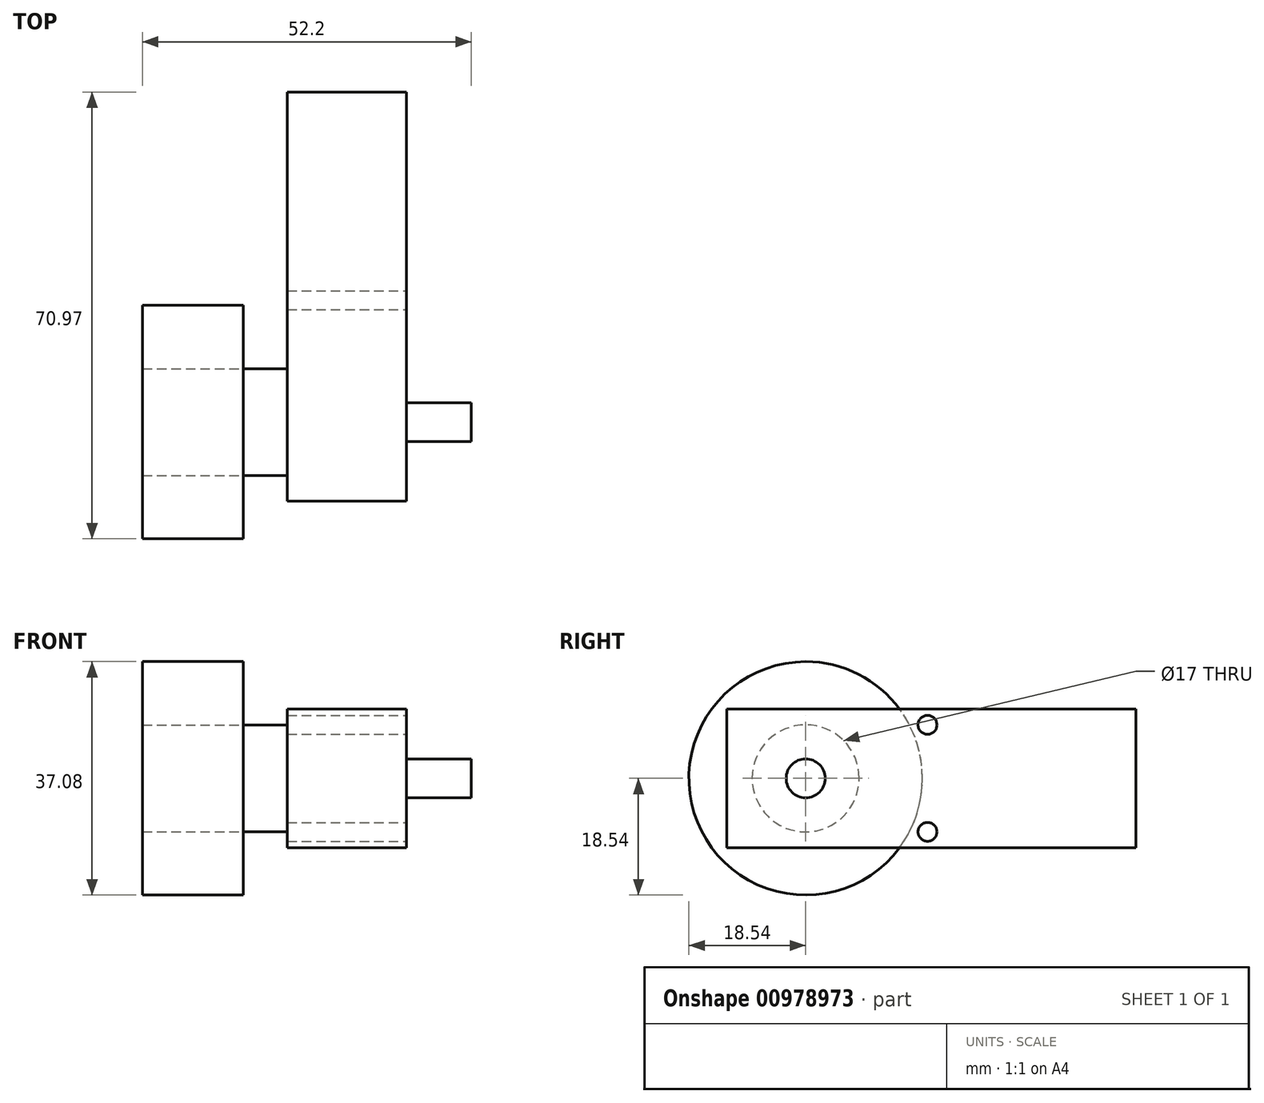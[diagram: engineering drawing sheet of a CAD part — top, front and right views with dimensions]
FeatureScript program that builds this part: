
annotation { "Feature Type Name" : "Feature", "Feature Type Description" : "" }
export const myFeature = defineFeature(function(context is Context, id is Id, definition is map)
    precondition{}
    {
        {
            var Q0;
            Q0=qCreatedBy(makeId("Top.planeOp"),FACE);
            var sketch = newSketch(context, id + "F0", { "sketchPlane" : qUnion([Q0])});
            skLineSegment(sketch, "E0.bottom", {"start": v(-11.97, 42.12) * mm, "end": v(6.93, 42.12) * mm});
            skLineSegment(sketch, "E0.top", {"start": v(-11.97, -22.86) * mm, "end": v(6.93, -22.86) * mm});
            skLineSegment(sketch, "E0.left", {"start": v(-11.97, 42.12) * mm, "end": v(-11.97, -22.86) * mm});
            skLineSegment(sketch, "E0.right", {"start": v(6.93, 42.12) * mm, "end": v(6.93, -22.86) * mm});
            skSolve(sketch);
        }
        {
            var Q0;
            Q0=makeQuery(id+"F0.imprint","IMPRINT",FACE,{"disambiguationData":[TD([[makeQuery(id+"F0.imprint","IMPRINT",EDGE,{"derivedFrom":sQuery(id+"F0.wireOp",EDGE,"E0.bottom")}),-1.0]])]});
            extrude(context, id + "F1", {"entities" : qUnion([Q0]), "depth" : 22 * mm, "offsetDistance" : 25 * mm});
        }
        {
            var Q0;
            Q0=makeQuery(id+"F1.opExtrude","SWEPT_FACE",FACE,{"disambiguationData":[OSD([sQuery(id+"F0.wireOp",EDGE,"E0.left")])]});
            var sketch = newSketch(context, id + "F2", { "sketchPlane" : qUnion([Q0])});
            skCircle(sketch, "E1", {"center": v(10.31, 11) * mm, "radius": 8.5 * mm});
            skSolve(sketch);
        }
        {
            var Q0;
            Q0=makeQuery(id+"F2.imprint","IMPRINT",FACE,{"disambiguationData":[TD([[makeQuery(id+"F2.imprint","IMPRINT",EDGE,{"derivedFrom":sQuery(id+"F2.wireOp",EDGE,"E1")}),1.0]])]});
            extrude(context, id + "F3", {"entities" : qUnion([Q0]), "operationType" : NewBodyOperationType.ADD, "depth" : 7 * mm, "offsetDistance" : 25 * mm});
        }
        {
            var Q0;
            Q0=makeQuery(id+"F3.opExtrude","CAP_FACE",FACE,{"disambiguationData":[OSD([sQuery(id+"F2.wireOp",EDGE,"E1")])],"isStart":false});
            var sketch = newSketch(context, id + "F4", { "sketchPlane" : qUnion([Q0])});
            skCircle(sketch, "E2", {"center": v(10.31, 11) * mm, "radius": 18.54 * mm});
            skSolve(sketch);
        }
        {
            var Q0;
            Q0=makeQuery(id+"F4.imprint","IMPRINT",FACE,{"disambiguationData":[TD([[makeQuery(id+"F4.imprint","IMPRINT",EDGE,{"derivedFrom":sQuery(id+"F4.wireOp",EDGE,"E2")}),1.0]])]});
            extrude(context, id + "F5", {"entities" : qUnion([Q0]), "depth" : 16 * mm, "offsetDistance" : 25 * mm});
        }
        {
            var Q0;
            Q0=makeQuery(id+"F5.opExtrude","CAP_FACE",FACE,{"disambiguationData":[OSD([sQuery(id+"F2.wireOp",EDGE,"E1"),sQuery(id+"F4.wireOp",EDGE,"E2")])],"isStart":true});
            var sketch = newSketch(context, id + "F6", { "sketchPlane" : qUnion([Q0])});
            skCircle(sketch, "E3", {"center": v(-10.31, 11) * mm, "radius": 3.1 * mm});
            skSolve(sketch);
        }
        {
            var Q0;
            Q0=qSketchRegion(id+"F6",true);
            extrude(context, id + "F7", {"entities" : qUnion([Q0]), "operationType" : NewBodyOperationType.ADD, "depth" : 36.2 * mm, "offsetDistance" : 25 * mm});
        }
        {
            var Q0;
            Q0=makeQuery(id+"F1.opExtrude","SWEPT_FACE",FACE,{"disambiguationData":[OSD([sQuery(id+"F0.wireOp",EDGE,"E0.right")])]});
            var sketch = newSketch(context, id + "F8", { "sketchPlane" : qUnion([Q0])});
            skLineSegment(sketch, "E4", {"start": v(-22.86, 22) * mm, "end": v(10.54, 22) * mm});
            skCircle(sketch, "E5", {"center": v(9.04, 2.5) * mm, "radius": 1.5 * mm});
            skCircle(sketch, "E6", {"center": v(9.04, 19.5) * mm, "radius": 1.5 * mm});
            skSolve(sketch);
        }
        {
            var Q0;
            Q0=sQuery(id+"F8.wireOp",VERTEX,"E5.center");
            var Q1;
            Q1=sQuery(id+"F8.wireOp",VERTEX,"E6.center");
            var Q2;
            Q2=makeQuery(id+"F1.opExtrude","SWEPT_BODY",BODY,{"disambiguationData":[OSD([sQuery(id+"F0.wireOp",EDGE,"E0.bottom"),sQuery(id+"F0.wireOp",EDGE,"E0.top"),sQuery(id+"F0.wireOp",EDGE,"E0.left"),sQuery(id+"F0.wireOp",EDGE,"E0.right")])]});
            hole(context, id + "F9", {"style" : HoleStyle.SIMPLE, "endStyle" : HoleEndStyle.THROUGH, "holeDiameter" : 3 * mm, "majorDiameter" : 5 * mm, "isTappedThrough" : true, "tappedDepth" : 12 * mm, "tapClearance" : 3, "locations" : qUnion([Q0, Q1]), "scope" : qUnion([Q2])});
        }
    });
